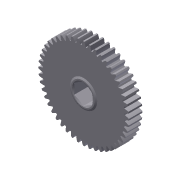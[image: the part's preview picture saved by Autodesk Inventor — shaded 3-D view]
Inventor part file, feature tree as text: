
AUTODESK INVENTOR PART (.ipt)
format: ipt  version: 2011 (Build 150239000, 239)  size: 368,128 bytes
history: native  units: mm (DEFAULTED — no unit token found)
features: sketch x5, other x4, extrude x3, plane x3, revolve x1, projected_geometry x1
ambient origin geometry x8: Origin, YZ Plane, XZ Plane, XY Plane, X Axis, Y Axis, Z Axis, Center Point
bodies: Solid1 (feature_tree)
feature tree (17):
  other  "Gear 48T 20dp 500hex"
  extrude  "Extrusion1"  Depth=9.525mm TaperAngle=0.0deg
  plane  "Work Plane1"
  plane  "Work Plane2"
  plane  "Work Plane3"
  other  "Spur Gear"
  extrude  "Extrusion2"  Depth=76.2mm TaperAngle=0.0deg
  extrude  "Extrusion3"  TaperAngle=0.0deg  [1 undecoded]
  revolve  "Revolution1"  [1 undecoded]
  sketch  "Sketch1"  dims[d0=63.5mm d1=9.525mm d2=0.0mm]
  sketch  "Sketch2"  dims[d3=60.96mm d4=76.2mm d5=0.0mm]
  other  "Srf1"
  sketch  "Sketch3"  dims[d6=0.0mm d7=0.654498mm d9=0.0mm]
  sketch  "Sketch4"  dims[d14=0.0mm d15=152.4mm d16=0.0mm]
  sketch  "Sketch5"  dims[d17=0.0mm d18=0.0mm d19=152.4mm d20=19.05mm d21=0.635mm d22=0.0mm d23=12.7mm d24=0.635mm d25=0.0mm d26=1.143mm d27=0.889mm d28=5.148721mm d29=2.54mm d30=90.0deg]
  other  "Pitch Diameter"
  projected_geometry  "Project Cut Edges1"
note: 2 required parameter values undecoded (feature->parameter linkage not recoverable at this tier; creation-order binding heuristic only, values carry confidence <= 0.55)